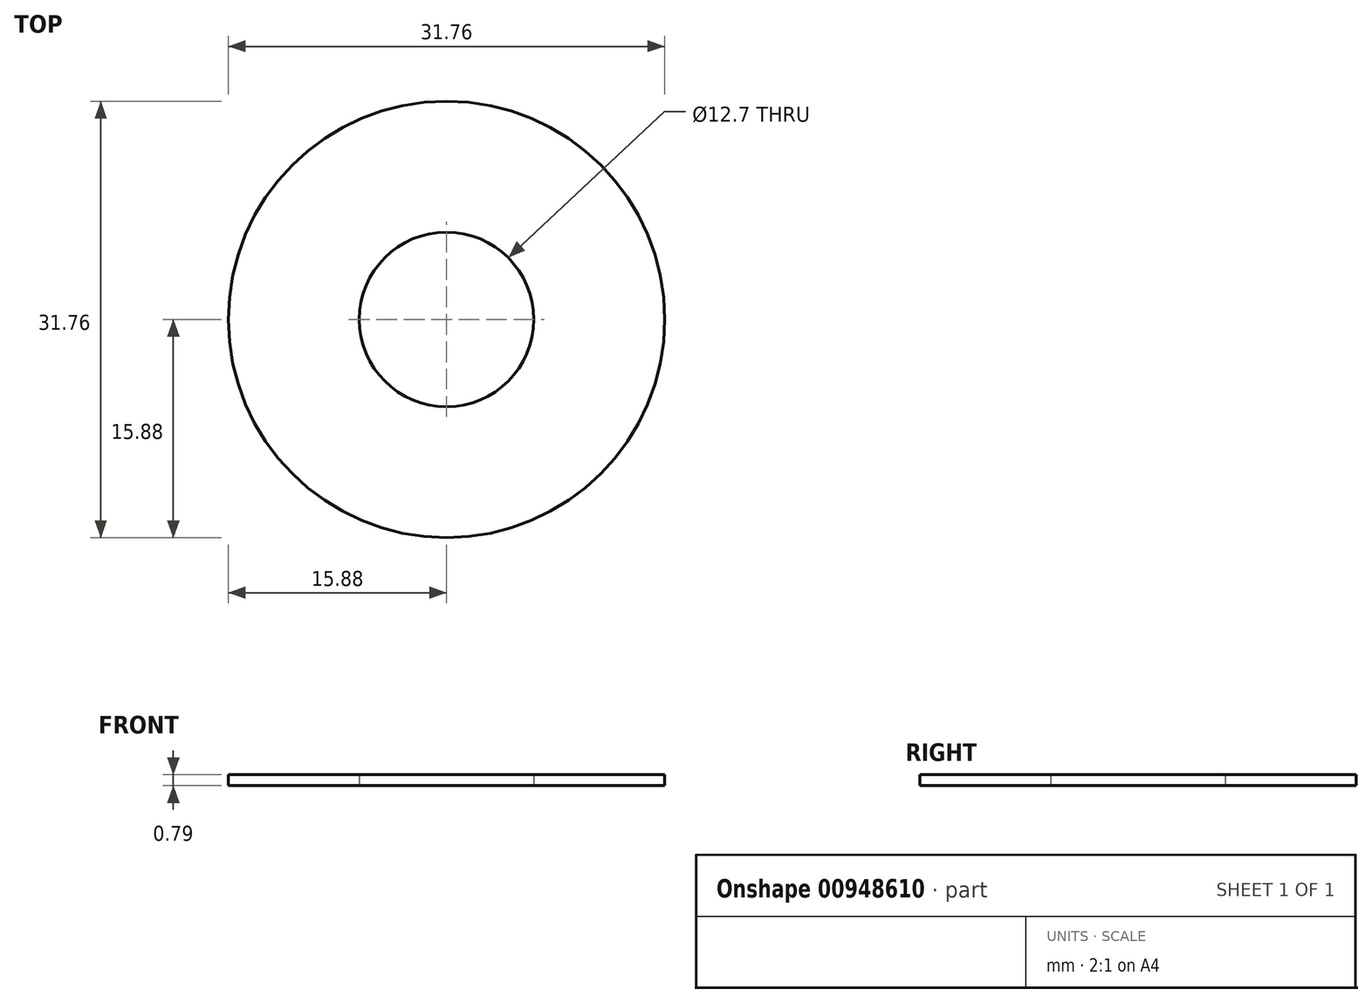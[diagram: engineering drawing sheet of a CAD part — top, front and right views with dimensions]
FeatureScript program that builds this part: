
annotation { "Feature Type Name" : "Feature", "Feature Type Description" : "" }
export const myFeature = defineFeature(function(context is Context, id is Id, definition is map)
    precondition{}
    {
        {
            var Q0;
            Q0=qCreatedBy(makeId("Top.planeOp"),FACE);
            var sketch = newSketch(context, id + "F0", { "sketchPlane" : qUnion([Q0])});
            skCircle(sketch, "E0", {"center": v(0, 0) * mm, "radius": 15.88 * mm});
            skCircle(sketch, "E1", {"center": v(0, 0) * mm, "radius": 6.35 * mm});
            skSolve(sketch);
        }
        {
            var Q0;
            Q0 = qSketchRegion(id + "F0", true);
            extrude(context, id + "F1", {"entities" : qUnion([Q0]), "depth" : 0.8 * mm, "offsetDistance" : 25.4 * mm});
        }
    });
